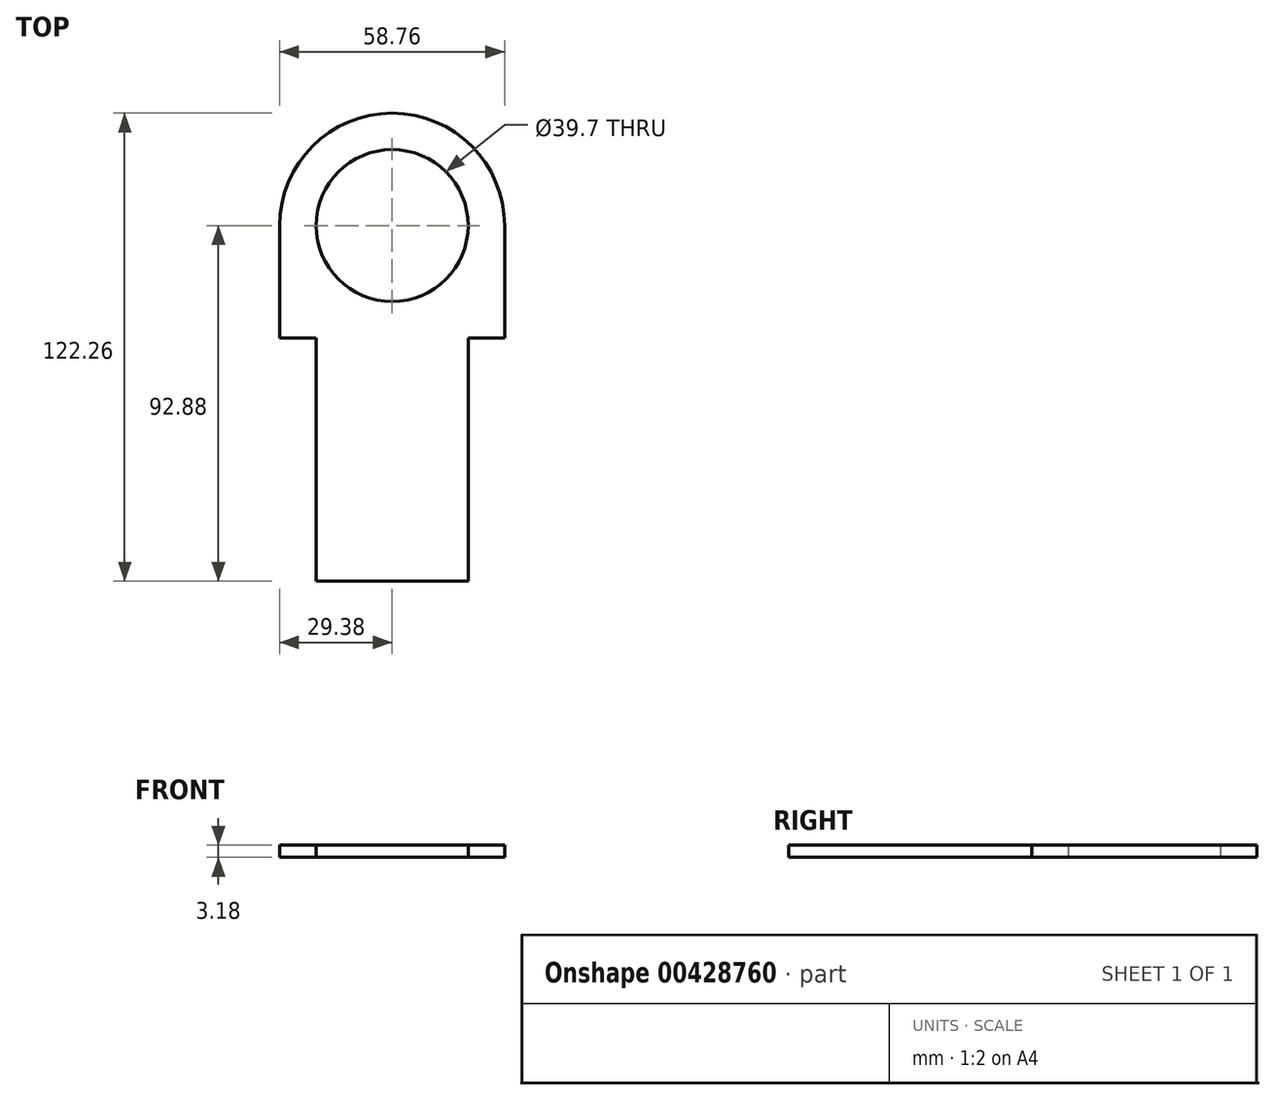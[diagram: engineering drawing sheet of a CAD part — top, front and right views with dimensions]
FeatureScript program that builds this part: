
annotation { "Feature Type Name" : "Feature", "Feature Type Description" : "" }
export const myFeature = defineFeature(function(context is Context, id is Id, definition is map)
    precondition{}
    {
        {
            var Q0;
            Q0=qCreatedBy(makeId("Top.planeOp"),FACE);
            var sketch = newSketch(context, id + "F0", { "sketchPlane" : qUnion([Q0])});
            skCircle(sketch, "E0", {"center": v(0, 0) * mm, "radius": 19.85 * mm});
            skLineSegment(sketch, "E1", {"start": v(0, 46.85) * mm, "end": v(0, -92.88) * mm, "construction": true});
            skLineSegment(sketch, "E2", {"start": v(-19.85, -92.88) * mm, "end": v(19.85, -92.88) * mm});
            skLineSegment(sketch, "E3", {"start": v(19.85, -92.88) * mm, "end": v(19.85, -29.38) * mm});
            skLineSegment(sketch, "E4", {"start": v(-19.85, -92.88) * mm, "end": v(-19.85, -29.38) * mm});
            skArc(sketch, "E5.0", {"start": v(29.38, 0) * mm, "mid": v(0, 29.38) * mm, "end": v(-29.38, 0) * mm});
            skLineSegment(sketch, "E6", {"start": v(29.38, 0) * mm, "end": v(29.38, -29.38) * mm});
            skLineSegment(sketch, "E7", {"start": v(-29.38, 0) * mm, "end": v(-29.38, -29.38) * mm});
            skLineSegment(sketch, "E8", {"start": v(19.85, -29.38) * mm, "end": v(29.38, -29.38) * mm});
            skLineSegment(sketch, "E9", {"start": v(-19.85, -29.38) * mm, "end": v(-29.38, -29.38) * mm});
            skLineSegment(sketch, "E10", {"start": v(-60.97, -19.85) * mm, "end": v(58.32, -19.85) * mm, "construction": true});
            skSolve(sketch);
        }
        {
            var Q0;
            Q0 = qSketchRegion(id + "F0", true);
            extrude(context, id + "F1", {"entities" : qUnion([Q0]), "depth" : 3.17 * mm});
        }
    });
